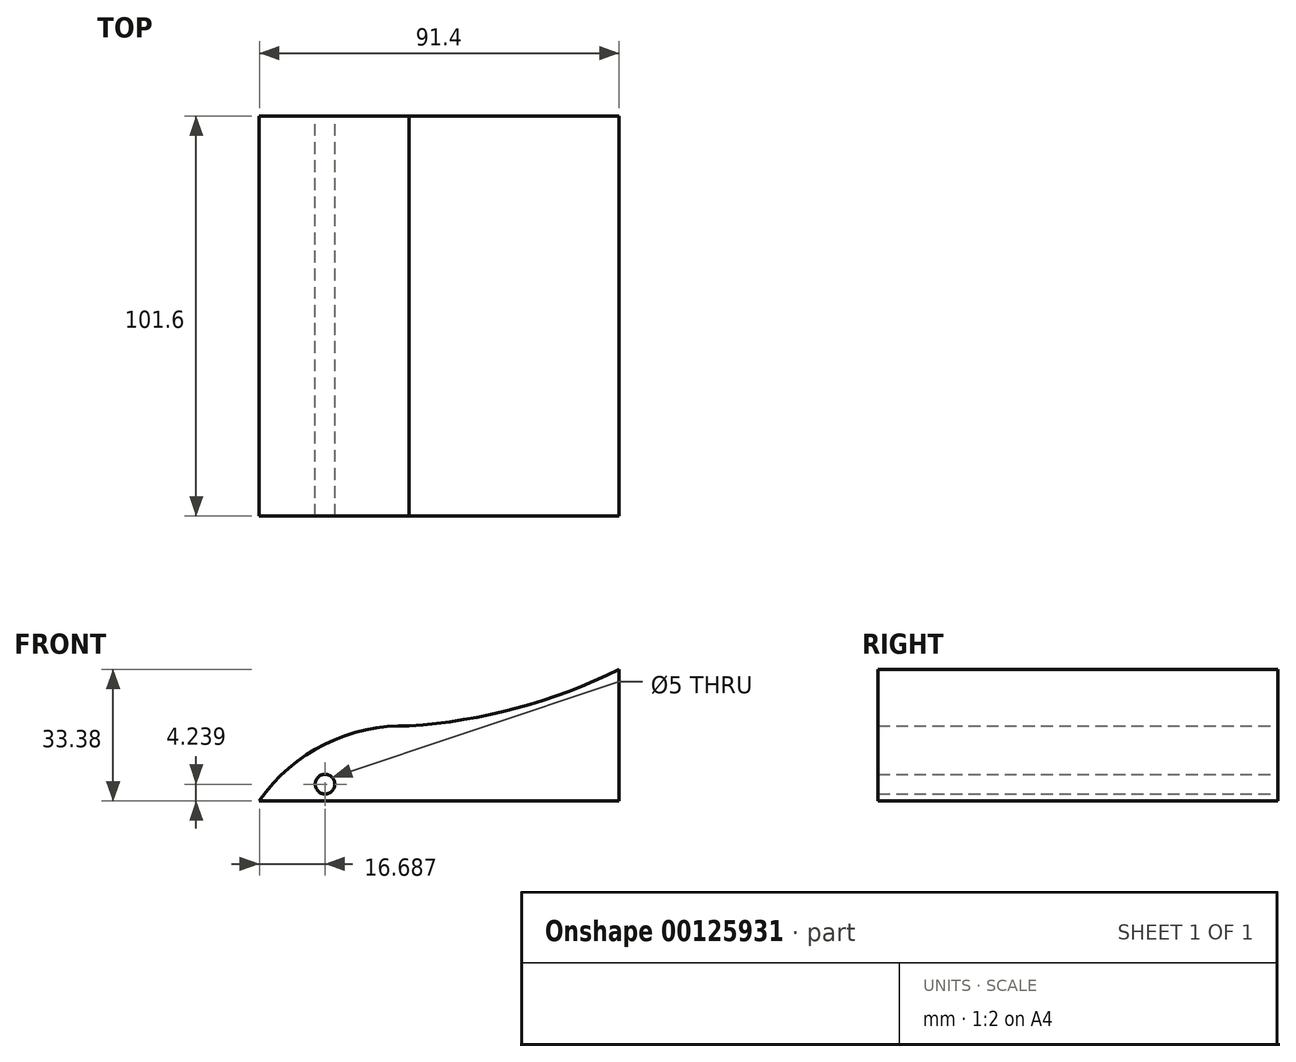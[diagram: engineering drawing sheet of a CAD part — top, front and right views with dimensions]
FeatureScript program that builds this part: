
annotation { "Feature Type Name" : "Feature", "Feature Type Description" : "" }
export const myFeature = defineFeature(function(context is Context, id is Id, definition is map)
    precondition{}
    {
        {
            var Q0;
            Q0=qCreatedBy(makeId("Front.planeOp"),FACE);
            var sketch = newSketch(context, id + "F0", { "sketchPlane" : qUnion([Q0])});
            skLineSegment(sketch, "E0", {"start": v(-62.52, 0) * mm, "end": v(-24.42, 0) * mm});
            skArc(sketch, "E1", {"start": v(-24.42, 19.05) * mm, "mid": v(-45.9, 14.38) * mm, "end": v(-62.52, 0) * mm});
            skArc(sketch, "E2", {"start": v(-24.42, 19.05) * mm, "mid": v(2.94, 23.56) * mm, "end": v(28.88, 33.38) * mm});
            skLineSegment(sketch, "E3", {"start": v(28.88, 33.38) * mm, "end": v(28.88, 0) * mm});
            skLineSegment(sketch, "E4", {"start": v(28.88, 0) * mm, "end": v(-24.42, 0) * mm});
            skCircle(sketch, "E5", {"center": v(-45.83, 4.24) * mm, "radius": 2.5 * mm});
            skSolve(sketch);
        }
        {
            var Q0;
            Q0=qSketchRegion(id+"F0",true);
            extrude(context, id + "F1", {"entities" : qUnion([Q0]), "depth" : 101.6 * mm});
        }
    });
